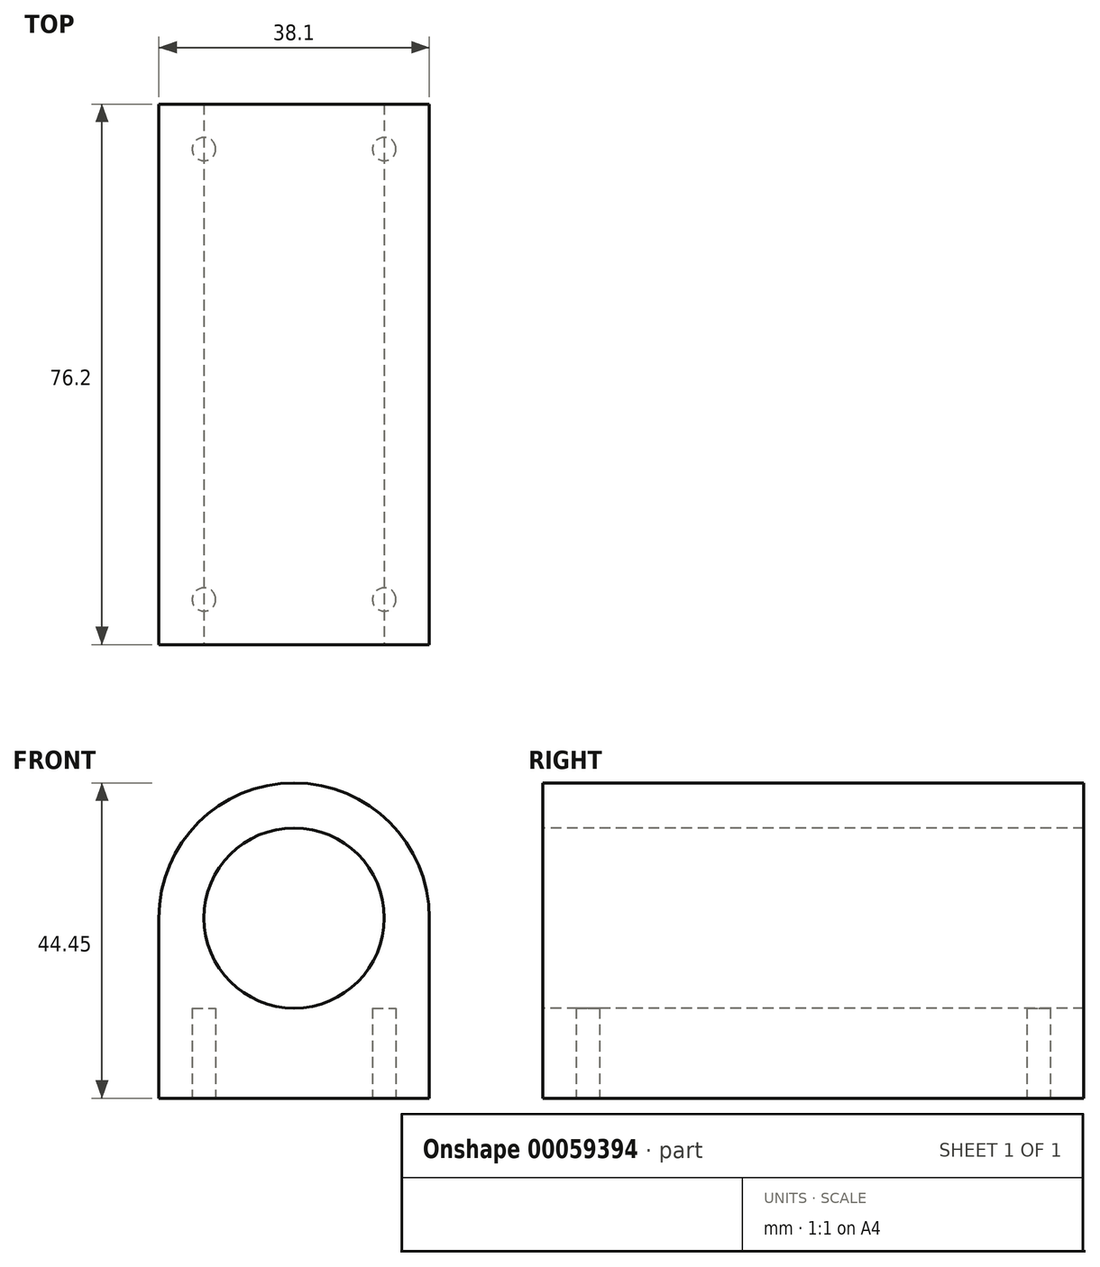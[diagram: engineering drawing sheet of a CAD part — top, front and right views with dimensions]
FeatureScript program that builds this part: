
annotation { "Feature Type Name" : "Feature", "Feature Type Description" : "" }
export const myFeature = defineFeature(function(context is Context, id is Id, definition is map)
    precondition{}
    {
        {
            var Q0;
            Q0=qCreatedBy(makeId("Front.planeOp"),FACE);
            var sketch = newSketch(context, id + "F0", { "sketchPlane" : qUnion([Q0])});
            skCircle(sketch, "E0", {"center": v(0, 0) * mm, "radius": 12.7 * mm});
            skArc(sketch, "E1", {"start": v(19.05, 0) * mm, "mid": v(0, 19.05) * mm, "end": v(-19.05, 0) * mm});
            skLineSegment(sketch, "E2", {"start": v(-19.05, 0) * mm, "end": v(-19.05, -25.4) * mm});
            skLineSegment(sketch, "E3", {"start": v(-19.05, -25.4) * mm, "end": v(19.05, -25.4) * mm});
            skLineSegment(sketch, "E4", {"start": v(19.05, 0) * mm, "end": v(19.05, -25.4) * mm});
            skSolve(sketch);
        }
        {
            var Q0;
            Q0 = qSketchRegion(id + "F0", true);
            extrude(context, id + "F1", {"entities" : qUnion([Q0]), "oppositeDirection" : true, "depth" : 76.2 * mm});
        }
        {
            var Q0;
            Q0=makeQuery(id+"F1.opExtrude","SWEPT_FACE",FACE,{"disambiguationData":[OSD([sQuery(id+"F0.wireOp",EDGE,"E3")])]});
            var sketch = newSketch(context, id + "F2", { "sketchPlane" : qUnion([Q0])});
            skLineSegment(sketch, "E5.bottom", {"start": v(-12.7, -6.35) * mm, "end": v(12.7, -6.35) * mm, "construction": true});
            skLineSegment(sketch, "E5.top", {"start": v(-12.7, -69.85) * mm, "end": v(12.7, -69.85) * mm, "construction": true});
            skLineSegment(sketch, "E5.left", {"start": v(-12.7, -6.35) * mm, "end": v(-12.7, -69.85) * mm, "construction": true});
            skLineSegment(sketch, "E5.right", {"start": v(12.7, -6.35) * mm, "end": v(12.7, -69.85) * mm, "construction": true});
            skCircle(sketch, "E6", {"center": v(-12.7, -6.35) * mm, "radius": 1.65 * mm});
            skCircle(sketch, "E7", {"center": v(12.7, -6.35) * mm, "radius": 1.65 * mm});
            skCircle(sketch, "E8", {"center": v(-12.7, -69.85) * mm, "radius": 1.65 * mm});
            skCircle(sketch, "E9", {"center": v(12.7, -69.85) * mm, "radius": 1.65 * mm});
            skSolve(sketch);
        }
        {
            var Q0;
            Q0 = qSketchRegion(id + "F2", true);
            extrude(context, id + "F3", {"entities" : qUnion([Q0]), "operationType" : NewBodyOperationType.REMOVE, "oppositeDirection" : true, "depth" : 12.7 * mm});
        }
    });
